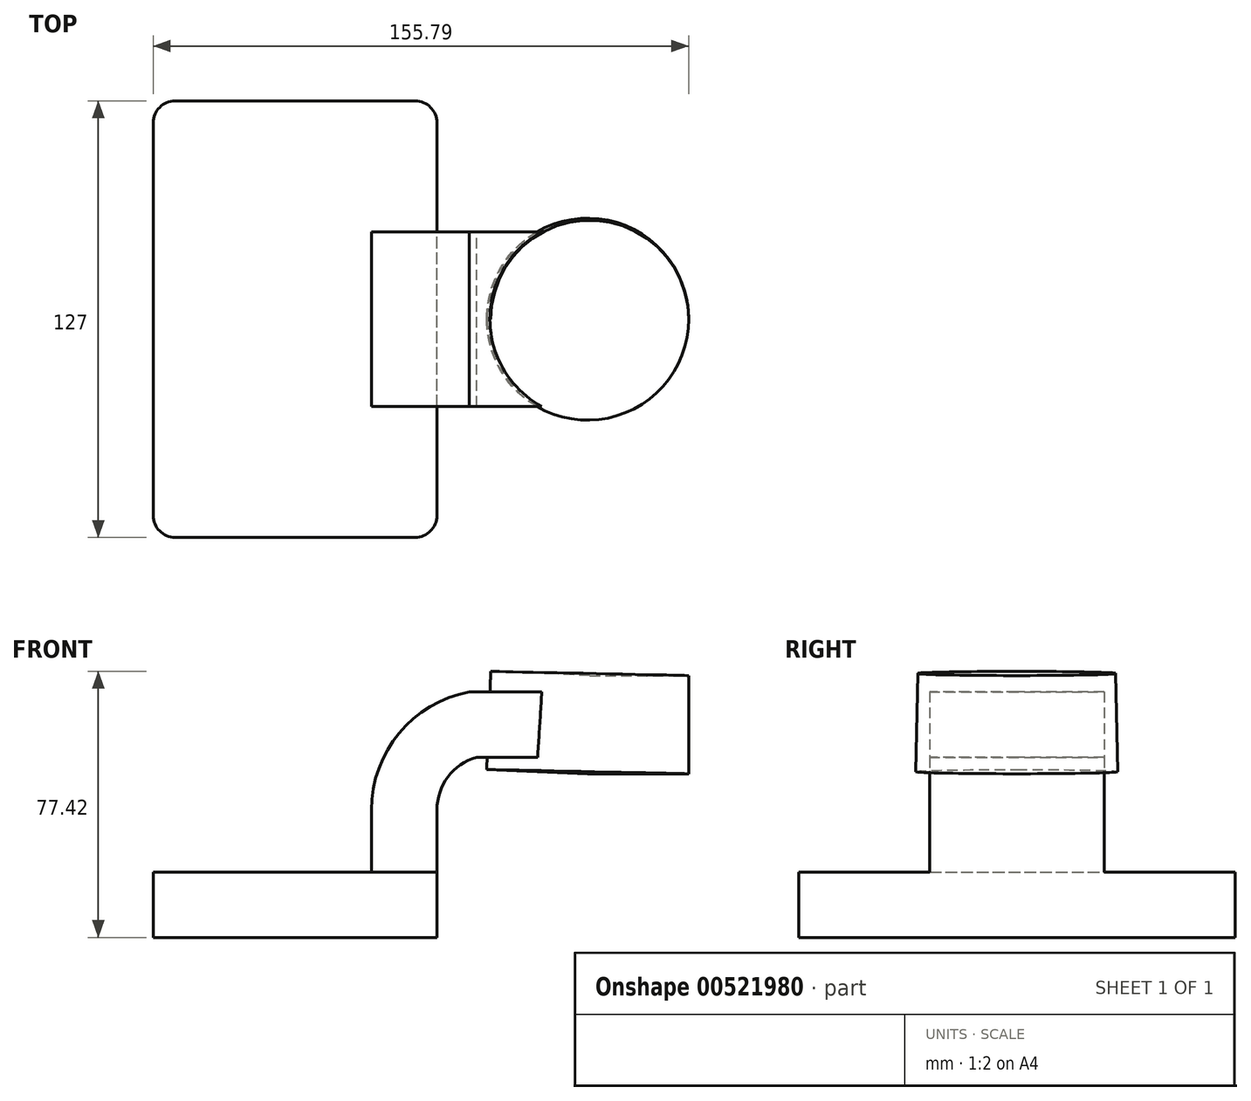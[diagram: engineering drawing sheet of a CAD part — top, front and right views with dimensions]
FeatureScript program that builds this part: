
annotation { "Feature Type Name" : "Feature", "Feature Type Description" : "" }
export const myFeature = defineFeature(function(context is Context, id is Id, definition is map)
    precondition{}
    {
        {
            var Q0;
            Q0=qCreatedBy(makeId("Front.planeOp"),FACE);
            var sketch = newSketch(context, id + "F0", { "sketchPlane" : qUnion([Q0])});
            skLineSegment(sketch, "E0.bottom", {"start": v(-41.28, 9.52) * mm, "end": v(41.28, 9.53) * mm});
            skLineSegment(sketch, "E0.top", {"start": v(-41.28, -9.53) * mm, "end": v(41.28, -9.53) * mm});
            skLineSegment(sketch, "E0.left", {"start": v(-41.28, 9.52) * mm, "end": v(-41.28, -9.53) * mm});
            skLineSegment(sketch, "E0.right", {"start": v(41.28, 9.53) * mm, "end": v(41.28, -9.52) * mm});
            skPoint(sketch, "E0.middle", {"position": v(0, 0) * mm});
            skLineSegment(sketch, "E1.bottom", {"start": v(63.72, 38.1) * mm, "end": v(114.52, 38.1) * mm});
            skLineSegment(sketch, "E1.top", {"start": v(63.72, 66.67) * mm, "end": v(114.52, 66.67) * mm});
            skLineSegment(sketch, "E1.left", {"start": v(63.72, 38.1) * mm, "end": v(63.72, 66.68) * mm});
            skLineSegment(sketch, "E1.right", {"start": v(114.52, 38.1) * mm, "end": v(114.52, 66.67) * mm});
            skPoint(sketch, "E1.middle", {"position": v(89.12, 52.39) * mm});
            skLineSegment(sketch, "E2", {"start": v(41.27, 9.53) * mm, "end": v(41.27, 27.6) * mm});
            skArc(sketch, "E3", {"start": v(41.28, 27.6) * mm, "mid": v(44.49, 37.18) * mm, "end": v(52.83, 42.88) * mm});
            skLineSegment(sketch, "E4", {"start": v(52.83, 42.88) * mm, "end": v(85.72, 42.88) * mm});
            skLineSegment(sketch, "E5.0", {"start": v(50.7, 61.93) * mm, "end": v(85.72, 61.93) * mm});
            skArc(sketch, "E5.1", {"start": v(22.23, 27.6) * mm, "mid": v(30.27, 49.9) * mm, "end": v(50.7, 61.93) * mm});
            skLineSegment(sketch, "E5.2", {"start": v(22.22, 9.53) * mm, "end": v(22.22, 27.6) * mm});
            skLineSegment(sketch, "E6", {"start": v(85.12, 38.1) * mm, "end": v(85.72, 66.67) * mm});
            skFitSpline(sketch, "E7", {"points": [v(-41.28, 9.52) * mm, v(50.7, 61.93) * mm], "startDerivative": vector(-1.8, 87.26) * mm, "endDerivative": vector(104.24, 0.6) * mm});
            skSolve(sketch);
        }
        {
            var Q0;
            Q0=makeQuery(id+"F0.imprint","IMPRINT",FACE,{"disambiguationData":[TD([[makeQuery(id+"F0.imprint","IMPRINT",EDGE,{"derivedFrom":sQuery(id+"F0.wireOp",EDGE,"E0.top")}),1.0]])]});
            extrude(context, id + "F1", {"entities" : qUnion([Q0]), "endBound" : BoundingType.SYMMETRIC, "depth" : 127 * mm, "offsetDistance" : 25.4 * mm});
        }
        {
            var Q0;
            {var subQ1=sQuery(id+"F0.wireOp",EDGE,"E2");Q0=makeQuery(id+"F0.imprint","IMPRINT",FACE,{"disambiguationData":[TD([[makeQuery(id+"F0.imprint","IMPRINT",EDGE,{"derivedFrom":subQ1}),1.0]])]});}
            var Q1;
            {var subQ0=sQuery(id+"F0.wireOp",EDGE,"E4");var subQ1=sQuery(id+"F0.wireOp",EDGE,"E1.left");var subQ2=makeQuery(id+"F0.imprint","INTERSECT",VERTEX,{"derivedFrom":[subQ1,subQ0]});Q1=makeQuery(id+"F0.imprint","IMPRINT",FACE,{"disambiguationData":[TD([[makeQuery(id+"F0.imprint","IMPRINT",EDGE,{"disambiguationData":[TD([[subQ2,-1.0]])],"derivedFrom":subQ1}),-1.0]])]});}
            extrude(context, id + "F2", {"entities" : qUnion([Q0, Q1]), "operationType" : NewBodyOperationType.ADD, "endBound" : BoundingType.SYMMETRIC, "depth" : 50.8 * mm, "offsetDistance" : 25.4 * mm});
        }
        {
            var Q0;
            Q0=makeQuery(id+"F0.imprint","IMPRINT",FACE,{"disambiguationData":[TD([[makeQuery(id+"F0.imprint","IMPRINT",EDGE,{"derivedFrom":sQuery(id+"F0.wireOp",EDGE,"E5.1")}),1.0]])]});
            extrude(context, id + "F3", {"entities" : qUnion([Q0]), "operationType" : NewBodyOperationType.ADD, "endBound" : BoundingType.SYMMETRIC, "depth" : 15.88 * mm, "offsetDistance" : 25.4 * mm});
        }
        {
            var Q0;
            {var subQ0=sQuery(id+"F0.wireOp",EDGE,"E1.right");Q0=makeQuery(id+"F0.imprint","IMPRINT",FACE,{"disambiguationData":[TD([[makeQuery(id+"F0.imprint","IMPRINT",EDGE,{"derivedFrom":subQ0}),1.0]])]});}
            var Q1;
            Q1=sQuery(id+"F0.wireOp",EDGE,"E6");
            revolve(context, id + "F4", {"operationType" : NewBodyOperationType.ADD, "entities" : qUnion([Q0]), "axis" : qUnion([Q1]), "revolveType" : RevolveType.FULL});
        }
        {
            var Q0;
            Q0=makeQuery(id+"F1.opExtrude","CAP_EDGE",EDGE,{"disambiguationData":[OSD([sQuery(id+"F0.wireOp",EDGE,"E0.left")])],"isStart":false});
            var Q1;
            Q1=makeQuery(id+"F1.opExtrude","CAP_EDGE",EDGE,{"disambiguationData":[OSD([sQuery(id+"F0.wireOp",EDGE,"E0.right")])],"isStart":false});
            var Q2;
            Q2=makeQuery(id+"F1.opExtrude","CAP_EDGE",EDGE,{"disambiguationData":[OSD([sQuery(id+"F0.wireOp",EDGE,"E0.right")])],"isStart":true});
            var Q3;
            Q3=makeQuery(id+"F1.opExtrude","CAP_EDGE",EDGE,{"disambiguationData":[OSD([sQuery(id+"F0.wireOp",EDGE,"E0.left")])],"isStart":true});
            fillet(context, id + "F5", {"entities" : qUnion([Q0, Q1, Q2, Q3]), "radius" : 6.35 * mm, "tangentPropagation" : true, "allowEdgeOverflow" : false});
        }
    });
